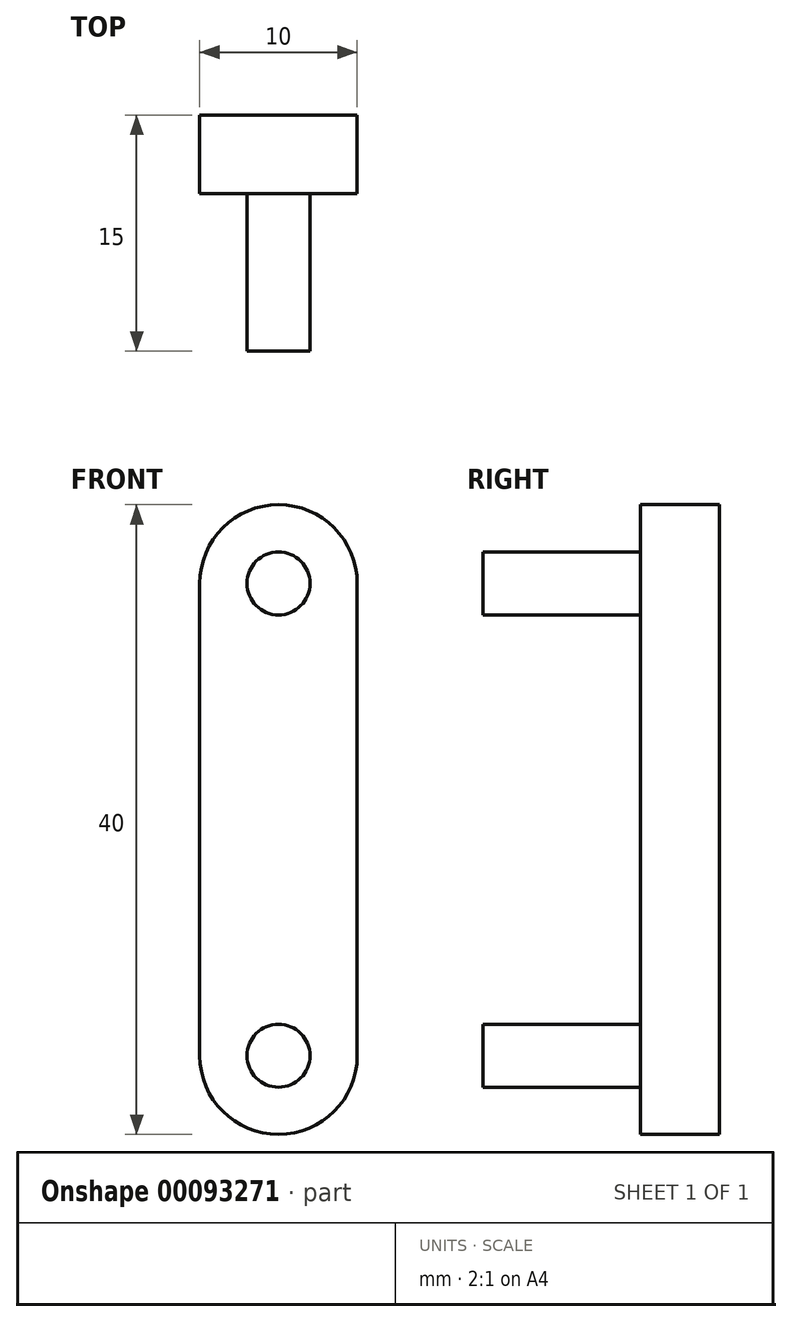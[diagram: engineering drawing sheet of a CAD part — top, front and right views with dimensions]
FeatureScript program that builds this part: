
annotation { "Feature Type Name" : "Feature", "Feature Type Description" : "" }
export const myFeature = defineFeature(function(context is Context, id is Id, definition is map)
    precondition{}
    {
        {
            var Q0;
            Q0=qCreatedBy(makeId("Front.planeOp"),FACE);
            var sketch = newSketch(context, id + "F0", { "sketchPlane" : qUnion([Q0])});
            skLineSegment(sketch, "E0.bottom", {"start": v(-5, 15) * mm, "end": v(5, 15) * mm});
            skLineSegment(sketch, "E0.top", {"start": v(-5, -15) * mm, "end": v(5, -15) * mm});
            skLineSegment(sketch, "E0.left", {"start": v(-5, 15) * mm, "end": v(-5, -15) * mm});
            skLineSegment(sketch, "E0.right", {"start": v(5, 15) * mm, "end": v(5, -15) * mm});
            skPoint(sketch, "E0.middle", {"position": v(0, 0) * mm});
            skArc(sketch, "E1", {"start": v(-5, 15) * mm, "mid": v(0, 20) * mm, "end": v(5, 15) * mm});
            skArc(sketch, "E2", {"start": v(-5, -15) * mm, "mid": v(0, -20) * mm, "end": v(5, -15) * mm});
            skSolve(sketch);
        }
        {
            var Q0;
            Q0=makeQuery(id+"F0.imprint","IMPRINT",FACE,{"disambiguationData":[TD([[makeQuery(id+"F0.imprint","IMPRINT",EDGE,{"derivedFrom":sQuery(id+"F0.wireOp",EDGE,"E0.top")}),-1.0]])]});
            var Q1;
            Q1=makeQuery(id+"F0.imprint","IMPRINT",FACE,{"disambiguationData":[TD([[makeQuery(id+"F0.imprint","IMPRINT",EDGE,{"derivedFrom":sQuery(id+"F0.wireOp",EDGE,"E0.bottom")}),1.0]])]});
            var Q2;
            Q2=makeQuery(id+"F0.imprint","IMPRINT",FACE,{"disambiguationData":[TD([[makeQuery(id+"F0.imprint","IMPRINT",EDGE,{"derivedFrom":sQuery(id+"F0.wireOp",EDGE,"E0.bottom")}),-1.0]])]});
            extrude(context, id + "F1", {"entities" : qUnion([Q0, Q1, Q2]), "depth" : 5 * mm});
        }
        {
            var Q0;
            Q0=qCreatedBy(makeId("Front.planeOp"),FACE);
            var sketch = newSketch(context, id + "F2", { "sketchPlane" : qUnion([Q0])});
            skLineSegment(sketch, "E3", {"start": v(7.52, 15) * mm, "end": v(-10.58, 15) * mm});
            skLineSegment(sketch, "E4", {"start": v(6.14, -15) * mm, "end": v(-13.84, -15) * mm});
            skCircle(sketch, "E5", {"center": v(0, 15) * mm, "radius": 2 * mm});
            skPoint(sketch, "E5.centerSnap0", {"position": v(-1.53, 15) * mm});
            skCircle(sketch, "E6", {"center": v(0, -15) * mm, "radius": 2 * mm});
            skSolve(sketch);
        }
        {
            var Q0;
            {var subQ0=sQuery(id+"F2.wireOp",EDGE,"E5");var subQ1=sQuery(id+"F2.wireOp",EDGE,"E3");var subQ2=makeQuery(id+"F2.imprint","INTERSECT",VERTEX,{"disambiguationData":[OD(0.0)],"derivedFrom":[subQ1,subQ0]});Q0=makeQuery(id+"F2.imprint","IMPRINT",FACE,{"disambiguationData":[TD([[makeQuery(id+"F2.imprint","IMPRINT",EDGE,{"disambiguationData":[TD([[subQ2,1.0]])],"derivedFrom":subQ1}),1.0]])]});}
            var Q1;
            {var subQ0=sQuery(id+"F2.wireOp",EDGE,"E5");var subQ1=sQuery(id+"F2.wireOp",EDGE,"E3");var subQ2=makeQuery(id+"F2.imprint","INTERSECT",VERTEX,{"disambiguationData":[OD(0.0)],"derivedFrom":[subQ1,subQ0]});Q1=makeQuery(id+"F2.imprint","IMPRINT",FACE,{"disambiguationData":[TD([[makeQuery(id+"F2.imprint","IMPRINT",EDGE,{"disambiguationData":[TD([[subQ2,1.0]])],"derivedFrom":subQ1}),-1.0]])]});}
            var Q2;
            {var subQ0=sQuery(id+"F2.wireOp",EDGE,"E6");var subQ1=sQuery(id+"F2.wireOp",EDGE,"E4");var subQ2=makeQuery(id+"F2.imprint","INTERSECT",VERTEX,{"disambiguationData":[OD(0.0)],"derivedFrom":[subQ1,subQ0]});Q2=makeQuery(id+"F2.imprint","IMPRINT",FACE,{"disambiguationData":[TD([[makeQuery(id+"F2.imprint","IMPRINT",EDGE,{"disambiguationData":[TD([[subQ2,1.0]])],"derivedFrom":subQ1}),1.0]])]});}
            var Q3;
            {var subQ0=sQuery(id+"F2.wireOp",EDGE,"E6");var subQ1=sQuery(id+"F2.wireOp",EDGE,"E4");var subQ2=makeQuery(id+"F2.imprint","INTERSECT",VERTEX,{"disambiguationData":[OD(0.0)],"derivedFrom":[subQ1,subQ0]});Q3=makeQuery(id+"F2.imprint","IMPRINT",FACE,{"disambiguationData":[TD([[makeQuery(id+"F2.imprint","IMPRINT",EDGE,{"disambiguationData":[TD([[subQ2,1.0]])],"derivedFrom":subQ1}),-1.0]])]});}
            extrude(context, id + "F3", {"entities" : qUnion([Q0, Q1, Q2, Q3]), "operationType" : NewBodyOperationType.ADD, "depth" : 15 * mm});
        }
    });
